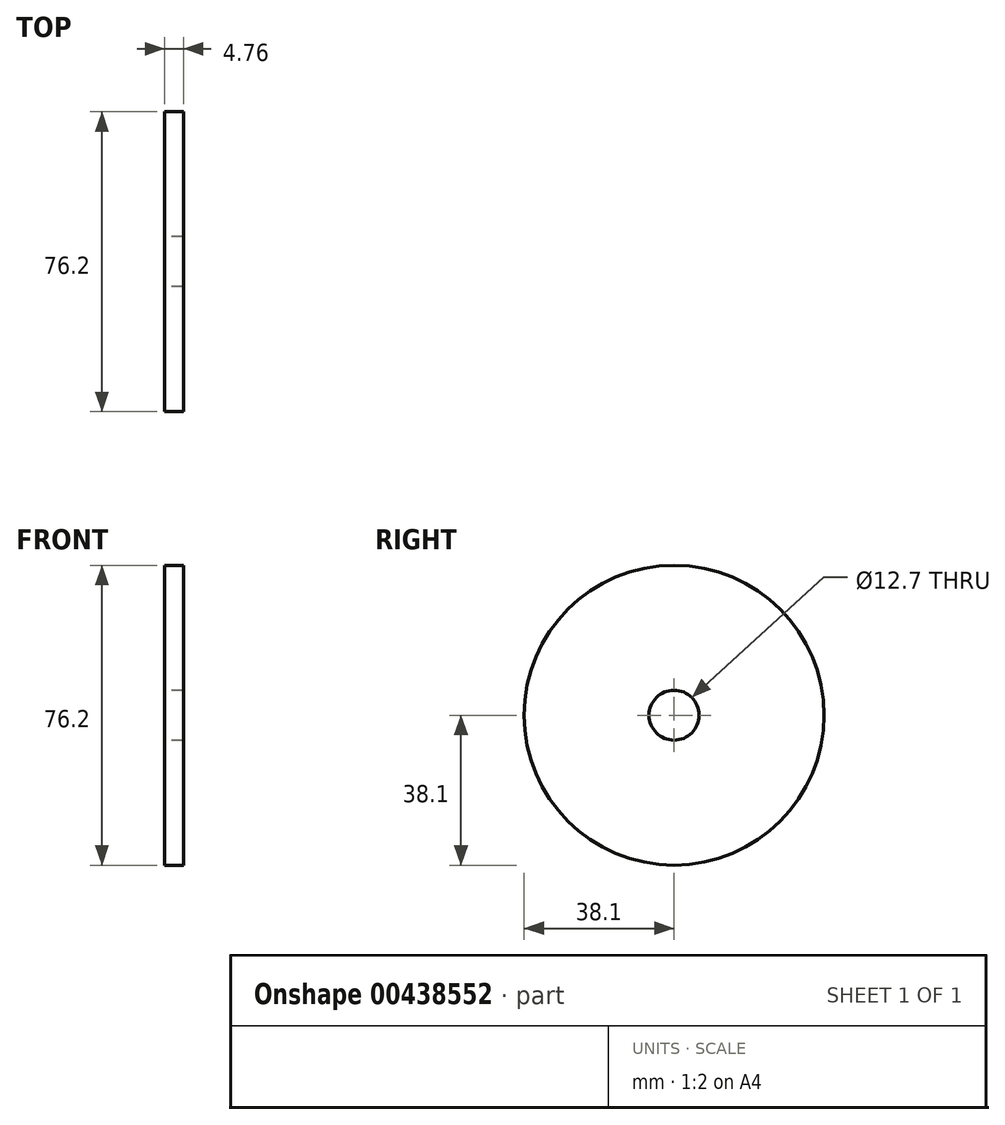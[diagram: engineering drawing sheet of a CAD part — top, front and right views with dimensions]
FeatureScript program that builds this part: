
annotation { "Feature Type Name" : "Feature", "Feature Type Description" : "" }
export const myFeature = defineFeature(function(context is Context, id is Id, definition is map)
    precondition{}
    {
        {
            var Q0;
            Q0=qCreatedBy(makeId("Right.planeOp"),FACE);
            var sketch = newSketch(context, id + "F0", { "sketchPlane" : qUnion([Q0])});
            skCircle(sketch, "E0", {"center": v(0, 0) * mm, "radius": 6.35 * mm});
            skCircle(sketch, "E1", {"center": v(0, 0) * mm, "radius": 38.1 * mm});
            skSolve(sketch);
        }
        {
            var Q0;
            Q0=makeQuery(id+"F0.imprint","IMPRINT",FACE,{"disambiguationData":[TD([[makeQuery(id+"F0.imprint","IMPRINT",EDGE,{"derivedFrom":sQuery(id+"F0.wireOp",EDGE,"E0")}),-1.0]])]});
            extrude(context, id + "F1", {"entities" : qUnion([Q0]), "depth" : 4.76 * mm});
        }
    });
